FCSTD DOCUMENT  (FreeCAD 0.14R3703 (Git))
Label: hullsTr
License: CC-BY 3.0
LicenseURL: http://creativecommons.org/licenses/by/3.0/
objects: Sketcher::SketchObject×7
note: 7 computed .brp shape members not serialized (recipe doc carries the construction recipe); baked Part::Feature solids carry a one-line shape summary decoded from their .brp

FEATURE [Sketcher::SketchObject] Sketch  label="stemline"
  Placement = pos=(0,0,0) rot=(0.57735,0.57735,0.57735;2.0944rad)
  sketch-geometry (3):
    g0: LineSegment StartX=32.4325 StartY=-0.36441 StartZ=0 EndX=13.9316 EndY=2.90478 EndZ=0
    g1: LineSegment StartX=13.9316 StartY=2.90478 StartZ=0 EndX=7.09176 EndY=7.00867 EndZ=0
    g2: LineSegment StartX=7.09176 StartY=7.00867 StartZ=0 EndX=2.75988 EndY=17.7244 EndZ=0
  constraints (2):
    c: Coincident(g0,g1)
    c: Coincident(g1,g2)
FEATURE [Sketcher::SketchObject] Sketch001  label="cs1"
  Placement = pos=(0,0,0) rot=(1,0,0;1.5708rad)
  sketch-geometry (3):
    g0: LineSegment StartX=1.90273 StartY=0 StartZ=0 EndX=6.36545 EndY=5.67264 EndZ=0
    g1: LineSegment StartX=6.36545 StartY=5.67264 StartZ=0 EndX=7.58101 EndY=11.5478 EndZ=0
    g2: LineSegment StartX=7.58101 StartY=11.5478 StartZ=0 EndX=7.58101 EndY=21.2723 EndZ=0
  constraints (2):
    c: Coincident(g0,g1)
    c: Coincident(g1,g2)
FEATURE [Sketcher::SketchObject] Sketch003  label="transomXY"
  Placement = pos=(0,-60,0) rot=(0,0,1;0rad)
  sketch-geometry (3):
    g0: LineSegment StartX=0.271818 StartY=-25.2791 StartZ=0 EndX=4.34909 EndY=-25.2791 EndZ=0
    g1: LineSegment StartX=4.34909 StartY=-25.2791 StartZ=0 EndX=10.0573 EndY=-23.1046 EndZ=0
    g2: LineSegment StartX=10.0573 StartY=-23.1046 StartZ=0 EndX=12.2318 EndY=-20.3864 EndZ=0
  constraints (2):
    c: Coincident(g0,g1)
    c: Coincident(g1,g2)
FEATURE [Sketcher::SketchObject] Sketch004  label="cs2"
  Placement = pos=(0,-20,0) rot=(1,0,0;1.5708rad)
  sketch-geometry (3):
    g0: LineSegment StartX=1.90273 StartY=0 StartZ=0 EndX=6.36545 EndY=5.67264 EndZ=0
    g1: LineSegment StartX=6.36545 StartY=5.67264 StartZ=0 EndX=7.58101 EndY=11.5478 EndZ=0
    g2: LineSegment StartX=7.58101 StartY=11.5478 StartZ=0 EndX=7.58101 EndY=21.2723 EndZ=0
  constraints (2):
    c: Coincident(g0,g1)
    c: Coincident(g1,g2)
FEATURE [Sketcher::SketchObject] Sketch005  label="cs3"
  Placement = pos=(0,-40,0) rot=(1,0,0;1.5708rad)
  sketch-geometry (3):
    g0: LineSegment StartX=1.90273 StartY=0 StartZ=0 EndX=6.36545 EndY=5.67264 EndZ=0
    g1: LineSegment StartX=6.36545 StartY=5.67264 StartZ=0 EndX=7.58101 EndY=11.5478 EndZ=0
    g2: LineSegment StartX=7.58101 StartY=11.5478 StartZ=0 EndX=7.58101 EndY=21.2723 EndZ=0
  constraints (2):
    c: Coincident(g0,g1)
    c: Coincident(g1,g2)
FEATURE [Sketcher::SketchObject] Sketch006  label="cs4"
  Placement = pos=(0,-60,0) rot=(1,0,0;1.5708rad)
  sketch-geometry (3):
    g0: LineSegment StartX=1.90273 StartY=0 StartZ=0 EndX=6.36545 EndY=5.67264 EndZ=0
    g1: LineSegment StartX=6.36545 StartY=5.67264 StartZ=0 EndX=7.58101 EndY=11.5478 EndZ=0
    g2: LineSegment StartX=7.58101 StartY=11.5478 StartZ=0 EndX=7.58101 EndY=21.2723 EndZ=0
  constraints (2):
    c: Coincident(g0,g1)
    c: Coincident(g1,g2)
FEATURE [Sketcher::SketchObject] Sketch007  label="cs5"
  Placement = pos=(0,-80,0) rot=(1,0,0;1.5708rad)
  sketch-geometry (3):
    g0: LineSegment StartX=1.90273 StartY=0 StartZ=0 EndX=6.36545 EndY=5.67264 EndZ=0
    g1: LineSegment StartX=6.36545 StartY=5.67264 StartZ=0 EndX=7.58101 EndY=11.5478 EndZ=0
    g2: LineSegment StartX=7.58101 StartY=11.5478 StartZ=0 EndX=7.58101 EndY=21.2723 EndZ=0
  constraints (2):
    c: Coincident(g0,g1)
    c: Coincident(g1,g2)
